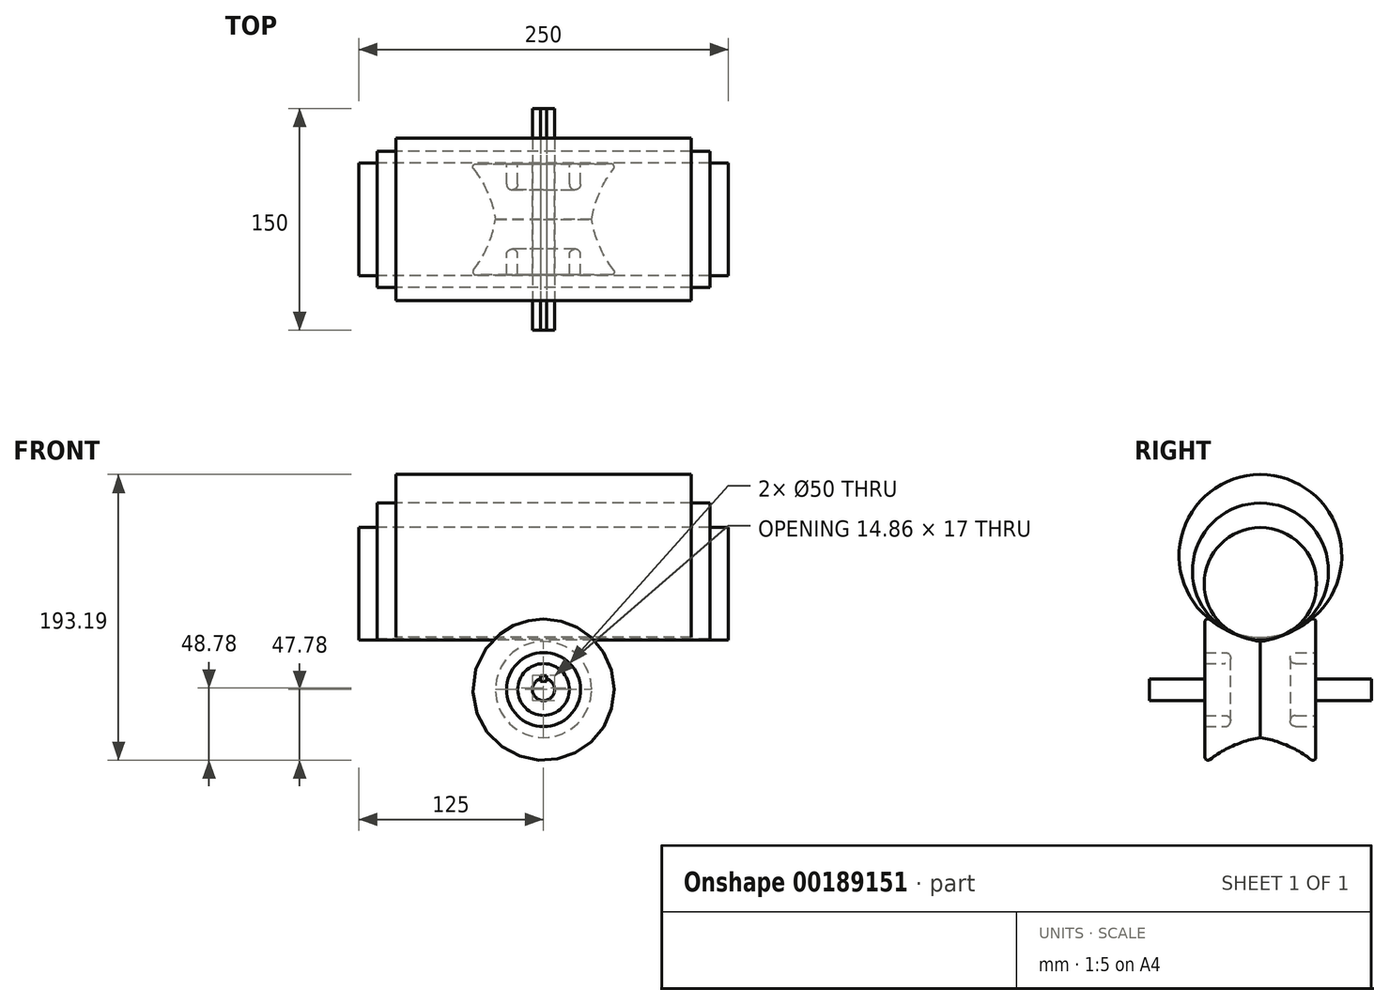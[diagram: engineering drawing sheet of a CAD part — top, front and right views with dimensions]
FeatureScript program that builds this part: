
annotation { "Feature Type Name" : "Feature", "Feature Type Description" : "" }
export const myFeature = defineFeature(function(context is Context, id is Id, definition is map)
    precondition{}
    {
        {
            var Q0;
            Q0=qCreatedBy(makeId("Right.planeOp"),FACE);
            var sketch = newSketch(context, id + "F0", { "sketchPlane" : qUnion([Q0])});
            skLineSegment(sketch, "E0", {"start": v(0, 7.5) * mm, "end": v(75, 7.5) * mm});
            skLineSegment(sketch, "E1", {"start": v(75, 7.5) * mm, "end": v(75, 0) * mm});
            skLineSegment(sketch, "E2.MirrorCS", {"start": v(0, 7.5) * mm, "end": v(-75, 7.5) * mm});
            skLineSegment(sketch, "E3.MirrorCS", {"start": v(-75, 7.5) * mm, "end": v(-75, 0) * mm});
            skLineSegment(sketch, "E4", {"start": v(-75, 0) * mm, "end": v(75, 0) * mm});
            skSolve(sketch);
        }
        {
            var Q0;
            Q0 = qSketchRegion(id + "F0", true);
            var Q1;
            Q1 = qSketchRegion(id + "F2", true);
            var Q2;
            Q2=sQuery(id+"F0.wireOp",EDGE,"E4");
            revolve(context, id + "F1", {"entities" : qUnion([Q0, Q1]), "axis" : qUnion([Q2]), "revolveType" : RevolveType.FULL});
        }
        {
            var Q0;
            Q0=makeQuery(id+"F1.opRevolve","SWEPT_FACE",FACE,{"disambiguationData":[OSD([sQuery(id+"F0.wireOp",EDGE,"E3.MirrorCS")])]});
            var sketch = newSketch(context, id + "F2", { "sketchPlane" : qUnion([Q0])});
            skLineSegment(sketch, "E5", {"start": v(0, 7.5) * mm, "end": v(0, 0) * mm, "construction": true});
            skLineSegment(sketch, "E6", {"start": v(2, 7.23) * mm, "end": v(2, 5.5) * mm});
            skLineSegment(sketch, "E7", {"start": v(0, 5.5) * mm, "end": v(2, 5.5) * mm});
            skLineSegment(sketch, "E8.MirrorCS", {"start": v(-2, 7.23) * mm, "end": v(-2, 5.5) * mm});
            skLineSegment(sketch, "E9.MirrorCS", {"start": v(0, 5.5) * mm, "end": v(-2, 5.5) * mm});
            skSolve(sketch);
        }
        {
            var Q0;
            Q0 = qSketchRegion(id + "F2", true);
            var Q1;
            {var subQ1=sQuery(id+"F2.wireOp",EDGE,"E6");Q1=makeQuery(id+"F2.imprint","IMPRINT",FACE,{"disambiguationData":[TD([[makeQuery(id+"F2.imprint","IMPRINT",EDGE,{"derivedFrom":subQ1}),-1.0]])]});}
            extrude(context, id + "F3", {"entities" : qUnion([Q0, Q1]), "operationType" : NewBodyOperationType.REMOVE, "endBound" : BoundingType.THROUGH_ALL, "oppositeDirection" : true, "depth" : 25 * mm});
        }
        {
            var Q0;
            Q0=qCreatedBy(makeId("Right.planeOp"),FACE);
            var sketch = newSketch(context, id + "F4", { "sketchPlane" : qUnion([Q0])});
            skLineSegment(sketch, "E10", {"start": v(0, 7.5) * mm, "end": v(37.5, 7.5) * mm});
            skLineSegment(sketch, "E11", {"start": v(37.5, 7.5) * mm, "end": v(37.5, 17.5) * mm});
            skLineSegment(sketch, "E12", {"start": v(37.5, 17.5) * mm, "end": v(23.83, 17.5) * mm});
            skLineSegment(sketch, "E13", {"start": v(23.83, 25) * mm, "end": v(37.5, 25) * mm});
            skLineSegment(sketch, "E14", {"start": v(37.5, 25) * mm, "end": v(37.5, 50) * mm});
            skArc(sketch, "E15", {"start": v(0, 32.5) * mm, "mid": v(19.96, 38.65) * mm, "end": v(37.5, 50) * mm});
            skArc(sketch, "E16", {"start": v(23.83, 25) * mm, "mid": v(20.08, 21.25) * mm, "end": v(23.83, 17.5) * mm});
            skArc(sketch, "E17.MirrorCS", {"start": v(0, 32.5) * mm, "mid": v(-19.96, 38.65) * mm, "end": v(-37.5, 50) * mm});
            skLineSegment(sketch, "E18.MirrorCS", {"start": v(-37.5, 25) * mm, "end": v(-37.5, 50) * mm});
            skArc(sketch, "E19.MirrorCS", {"start": v(-23.83, 25) * mm, "mid": v(-20.08, 21.25) * mm, "end": v(-23.83, 17.5) * mm});
            skLineSegment(sketch, "E20.MirrorCS", {"start": v(-23.83, 25) * mm, "end": v(-37.5, 25) * mm});
            skLineSegment(sketch, "E21.MirrorCS", {"start": v(-37.5, 17.5) * mm, "end": v(-23.83, 17.5) * mm});
            skLineSegment(sketch, "E22.MirrorCS", {"start": v(-37.5, 7.5) * mm, "end": v(-37.5, 17.5) * mm});
            skLineSegment(sketch, "E23.MirrorCS", {"start": v(0, 7.5) * mm, "end": v(-37.5, 7.5) * mm});
            skSolve(sketch);
        }
        {
            var Q0;
            Q0=makeQuery(id+"F4.imprint","IMPRINT",FACE,{"disambiguationData":[TD([[makeQuery(id+"F4.imprint","IMPRINT",EDGE,{"derivedFrom":sQuery(id+"F4.wireOp",EDGE,"E10")}),1.0]])]});
            var Q1;
            Q1=makeQuery(id+"F1.opRevolve","SWEPT_FACE",FACE,{"disambiguationData":[OSD([sQuery(id+"F0.wireOp",EDGE,"E0"),sQuery(id+"F0.wireOp",EDGE,"E2.MirrorCS")])]});
            revolve(context, id + "F5", {"entities" : qUnion([Q0]), "axis" : qUnion([Q1]), "revolveType" : RevolveType.FULL});
        }
        {
            var Q0;
            Q0=makeQuery(id+"F5.opRevolve","SWEPT_FACE",FACE,{"disambiguationData":[OSD([sQuery(id+"F4.wireOp",EDGE,"E22.MirrorCS")])]});
            var sketch = newSketch(context, id + "F6", { "sketchPlane" : qUnion([Q0])});
            skLineSegment(sketch, "E24", {"start": v(-2, 7.23) * mm, "end": v(-2, 9.5) * mm});
            skLineSegment(sketch, "E25", {"start": v(-2, 9.5) * mm, "end": v(2, 9.5) * mm});
            skLineSegment(sketch, "E26", {"start": v(2, 9.5) * mm, "end": v(2, 7.23) * mm});
            skLineSegment(sketch, "E27", {"start": v(0, 7.5) * mm, "end": v(-3.28, 7.5) * mm, "construction": true});
            skSolve(sketch);
        }
        {
            var Q0;
            Q0 = qSketchRegion(id + "F6", true);
            var Q1;
            {var subQ0=sQuery(id+"F6.wireOp",EDGE,"E24");Q1=makeQuery(id+"F6.imprint","IMPRINT",FACE,{"disambiguationData":[TD([[makeQuery(id+"F6.imprint","IMPRINT",EDGE,{"derivedFrom":subQ0}),-1.0]])]});}
            extrude(context, id + "F7", {"entities" : qUnion([Q0, Q1]), "operationType" : NewBodyOperationType.REMOVE, "endBound" : BoundingType.THROUGH_ALL, "oppositeDirection" : true, "depth" : 25 * mm});
        }
        {
            var Q0;
            Q0=makeQuery(id+"F5.opRevolve","SWEPT_EDGE",EDGE,{"disambiguationData":[OSD([sQuery(id+"F4.wireOp",EDGE,"E17.MirrorCS"),sQuery(id+"F4.wireOp",EDGE,"E18.MirrorCS")])]});
            var Q1;
            Q1=makeQuery(id+"F5.opRevolve","SWEPT_EDGE",EDGE,{"disambiguationData":[OSD([sQuery(id+"F4.wireOp",EDGE,"E14"),sQuery(id+"F4.wireOp",EDGE,"E15")])]});
            fillet(context, id + "F8", {"entities" : qUnion([Q0, Q1]), "radius" : 2 * mm, "tangentPropagation" : true, "allowEdgeOverflow" : false});
        }
        {
            var Q0;
            Q0=qCreatedBy(makeId("Right.planeOp"),FACE);
            var sketch = newSketch(context, id + "F9", { "sketchPlane" : qUnion([Q0])});
            skCircle(sketch, "E28", {"center": v(0, 71.52) * mm, "radius": 38 * mm});
            skSolve(sketch);
        }
        {
            var Q0;
            Q0=makeQuery(id+"F9.imprint","IMPRINT",FACE,{"disambiguationData":[TD([[makeQuery(id+"F9.imprint","IMPRINT",EDGE,{"derivedFrom":sQuery(id+"F9.wireOp",EDGE,"E28")}),1.0]])]});
            extrude(context, id + "F10", {"entities" : qUnion([Q0]), "endBound" : BoundingType.SYMMETRIC, "depth" : 250 * mm});
        }
        {
            var Q0;
            Q0=makeQuery(id+"F10.opExtrude","SWEPT_BODY",BODY,{"disambiguationData":[OSD([sQuery(id+"F9.wireOp",EDGE,"E28")])]});
            transform(context, id + "F11", {"entities" : qUnion([Q0]), "transformType" : TransformType.TRANSLATION_3D, "dx" : 0 * mm, "dy" : 0 * mm, "dz" : 0 * mm, "makeCopy" : true});
        }
        {
            var Q0;
            Q0=makeQuery(id+"F11.opPattern","COPY",BODY,{"derivedFrom":makeQuery(id+"F10.opExtrude","SWEPT_BODY",BODY,{"disambiguationData":[OSD([sQuery(id+"F9.wireOp",EDGE,"E28")])]}),"instanceName":"1"});
            deleteBodies(context, id + "F12", {"entities" : qUnion([Q0])});
        }
        {
            var Q0;
            Q0=qCreatedBy(makeId("Right.planeOp"),FACE);
            var sketch = newSketch(context, id + "F13", { "sketchPlane" : qUnion([Q0])});
            skCircle(sketch, "E29", {"center": v(0, 419.8) * mm, "radius": 46 * mm});
            skCircle(sketch, "E30", {"center": v(0, 80.1) * mm, "radius": 46 * mm});
            skSolve(sketch);
        }
        {
            var Q0;
            Q0 = qSketchRegion(id + "F13", true);
            extrude(context, id + "F14", {"entities" : qUnion([Q0]), "endBound" : BoundingType.SYMMETRIC, "depth" : 225 * mm});
        }
        {
            var Q0;
            Q0=makeQuery(id+"F14.opExtrude","SWEPT_BODY",BODY,{"disambiguationData":[OSD([sQuery(id+"F13.wireOp",EDGE,"E29")])]});
            deleteBodies(context, id + "F15", {"entities" : qUnion([Q0])});
        }
        {
            var Q0;
            Q0=qCreatedBy(makeId("Right.planeOp"),FACE);
            var sketch = newSketch(context, id + "F16", { "sketchPlane" : qUnion([Q0])});
            skCircle(sketch, "E31", {"center": v(0, 90.4) * mm, "radius": 55 * mm});
            skSolve(sketch);
        }
        {
            var Q0;
            Q0=makeQuery(id+"F16.imprint","IMPRINT",FACE,{"disambiguationData":[TD([[makeQuery(id+"F16.imprint","IMPRINT",EDGE,{"derivedFrom":sQuery(id+"F16.wireOp",EDGE,"E31")}),1.0]])]});
            extrude(context, id + "F17", {"entities" : qUnion([Q0]), "endBound" : BoundingType.SYMMETRIC, "depth" : 200 * mm});
        }
    });
